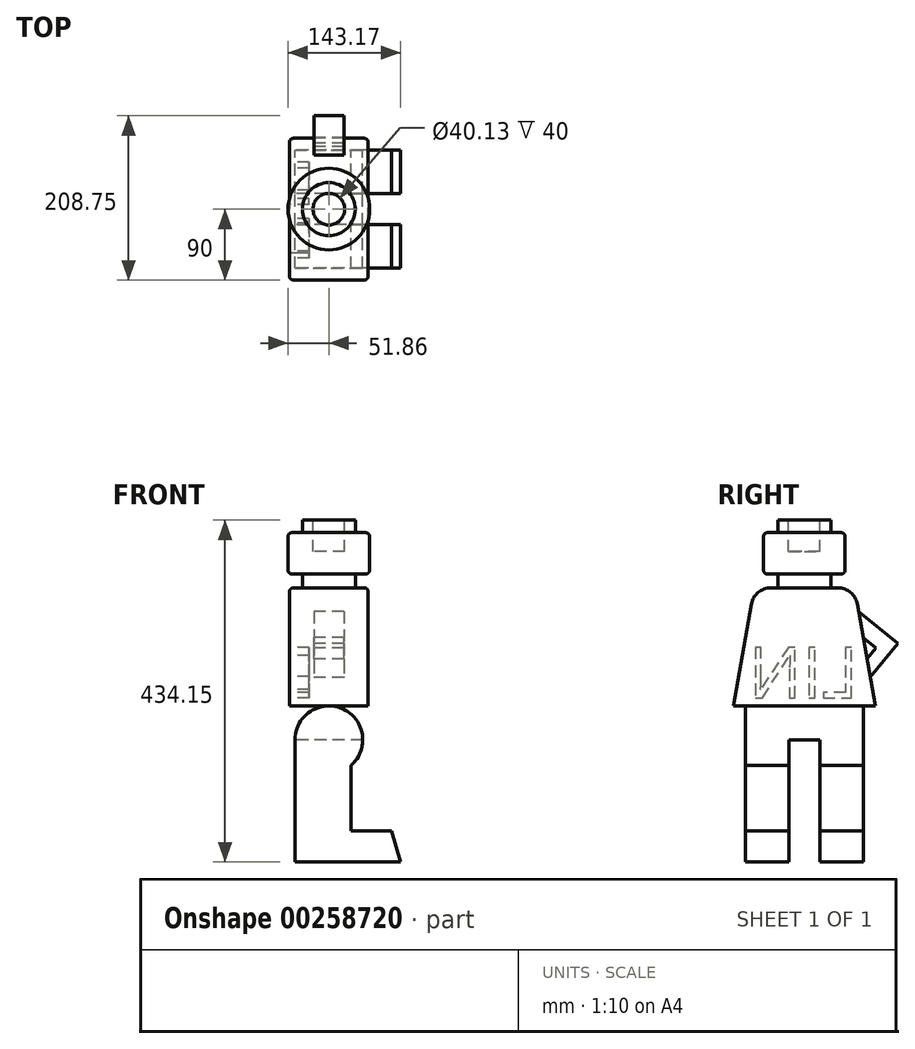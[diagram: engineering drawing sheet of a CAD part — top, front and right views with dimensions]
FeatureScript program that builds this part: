
annotation { "Feature Type Name" : "Feature", "Feature Type Description" : "" }
export const myFeature = defineFeature(function(context is Context, id is Id, definition is map)
    precondition{}
    {
        {
            var Q0;
            Q0=qCreatedBy(makeId("Front.planeOp"),FACE);
            var sketch = newSketch(context, id + "F0", { "sketchPlane" : qUnion([Q0])});
            skLineSegment(sketch, "E0", {"start": v(0, 41.34) * mm, "end": v(-33.6, 41.34) * mm});
            skLineSegment(sketch, "E1", {"start": v(-33.6, 41.34) * mm, "end": v(-33.6, 25.36) * mm});
            skLineSegment(sketch, "E2", {"start": v(-33.6, 25.36) * mm, "end": v(-51.86, 25.36) * mm});
            skLineSegment(sketch, "E3", {"start": v(-51.86, 25.36) * mm, "end": v(-51.86, -27.14) * mm});
            skLineSegment(sketch, "E4", {"start": v(-51.86, -27.14) * mm, "end": v(-33.6, -27.14) * mm});
            skLineSegment(sketch, "E5", {"start": v(-33.6, -27.14) * mm, "end": v(-33.6, -44.75) * mm});
            skLineSegment(sketch, "E6", {"start": v(-33.6, -44.75) * mm, "end": v(0, -44.75) * mm});
            skLineSegment(sketch, "E7", {"start": v(0, -44.75) * mm, "end": v(0, 41.34) * mm});
            skSolve(sketch);
        }
        {
            var Q0;
            Q0=makeQuery(id+"F0.imprint","IMPRINT",FACE,{"disambiguationData":[TD([[makeQuery(id+"F0.imprint","IMPRINT",EDGE,{"derivedFrom":sQuery(id+"F0.wireOp",EDGE,"E0")}),1.0]])]});
            var Q1;
            Q1=sQuery(id+"F0.wireOp",EDGE,"E7");
            revolve(context, id + "F1", {"entities" : qUnion([Q0]), "axis" : qUnion([Q1]), "revolveType" : RevolveType.FULL});
        }
        {
            var Q0;
            Q0=makeQuery(id+"F1.opRevolve","SWEPT_EDGE",EDGE,{"disambiguationData":[OSD([sQuery(id+"F0.wireOp",EDGE,"E2"),sQuery(id+"F0.wireOp",EDGE,"E3")])]});
            fillet(context, id + "F2", {"entities" : qUnion([Q0]), "radius" : 5 * mm, "tangentPropagation" : true, "allowEdgeOverflow" : false});
        }
        {
            var Q0;
            Q0=makeQuery(id+"F1.opRevolve","SWEPT_EDGE",EDGE,{"disambiguationData":[OSD([sQuery(id+"F0.wireOp",EDGE,"E3"),sQuery(id+"F0.wireOp",EDGE,"E4")])]});
            fillet(context, id + "F3", {"entities" : qUnion([Q0]), "radius" : 5 * mm, "tangentPropagation" : true, "allowEdgeOverflow" : false});
        }
        {
            var Q0;
            Q0=makeQuery(id+"F1.opRevolve","SWEPT_FACE",FACE,{"disambiguationData":[OSD([sQuery(id+"F0.wireOp",EDGE,"E0")])]});
            var sketch = newSketch(context, id + "F4", { "sketchPlane" : qUnion([Q0])});
            skCircle(sketch, "E8", {"center": v(0, 0) * mm, "radius": 20.06 * mm});
            skSolve(sketch);
        }
        {
            var Q0;
            Q0=makeQuery(id+"F4.imprint","IMPRINT",FACE,{"disambiguationData":[TD([[makeQuery(id+"F4.imprint","IMPRINT",EDGE,{"derivedFrom":sQuery(id+"F4.wireOp",EDGE,"E8")}),1.0]])]});
            extrude(context, id + "F5", {"entities" : qUnion([Q0]), "operationType" : NewBodyOperationType.REMOVE, "oppositeDirection" : true, "depth" : 40 * mm});
        }
        {
            var Q0;
            Q0=qCreatedBy(makeId("Right.planeOp"),FACE);
            var sketch = newSketch(context, id + "F6", { "sketchPlane" : qUnion([Q0])});
            skLineSegment(sketch, "E9.0", {"start": v(33.6, 41.34) * mm, "end": v(-33.6, 41.34) * mm});
            skLineSegment(sketch, "E10.0", {"start": v(33.6, -44.75) * mm, "end": v(-33.6, -44.75) * mm});
            skLineSegment(sketch, "E11", {"start": v(33.6, -44.75) * mm, "end": v(63.6, -44.75) * mm});
            skLineSegment(sketch, "E12", {"start": v(63.6, -44.75) * mm, "end": v(90, -194.47) * mm});
            skLineSegment(sketch, "E13", {"start": v(90, -194.47) * mm, "end": v(-90, -194.47) * mm});
            skLineSegment(sketch, "E14", {"start": v(-90, -194.47) * mm, "end": v(-63.6, -44.75) * mm});
            skLineSegment(sketch, "E15", {"start": v(-63.6, -44.75) * mm, "end": v(-33.6, -44.75) * mm});
            skSolve(sketch);
        }
        {
            var Q0;
            Q0=makeQuery(id+"F6.imprint","IMPRINT",FACE,{"disambiguationData":[TD([[makeQuery(id+"F6.imprint","IMPRINT",EDGE,{"derivedFrom":sQuery(id+"F6.wireOp",EDGE,"E10.0")}),1.0]])]});
            extrude(context, id + "F7", {"entities" : qUnion([Q0]), "endBound" : BoundingType.SYMMETRIC, "depth" : 100 * mm});
        }
        {
            var Q0;
            Q0=makeQuery(id+"F7.opExtrude","SWEPT_EDGE",EDGE,{"disambiguationData":[OSD([sQuery(id+"F6.wireOp",EDGE,"E14"),sQuery(id+"F6.wireOp",EDGE,"E15")])]});
            fillet(context, id + "F8", {"entities" : qUnion([Q0]), "radius" : 25 * mm, "tangentPropagation" : true, "allowEdgeOverflow" : false});
        }
        {
            var Q0;
            Q0=makeQuery(id+"F7.opExtrude","SWEPT_EDGE",EDGE,{"disambiguationData":[OSD([sQuery(id+"F6.wireOp",EDGE,"E11"),sQuery(id+"F6.wireOp",EDGE,"E12")])]});
            fillet(context, id + "F9", {"entities" : qUnion([Q0]), "radius" : 25 * mm, "tangentPropagation" : true, "allowEdgeOverflow" : false});
        }
        {
            var Q0;
            Q0=makeQuery(id+"F7.opExtrude","CAP_EDGE",EDGE,{"disambiguationData":[OSD([sQuery(id+"F6.wireOp",EDGE,"E10.0"),sQuery(id+"F6.wireOp",EDGE,"E11"),sQuery(id+"F6.wireOp",EDGE,"E15")])],"isStart":false});
            var Q1;
            Q1=makeQuery(id+"F7.opExtrude","CAP_EDGE",EDGE,{"disambiguationData":[OSD([sQuery(id+"F6.wireOp",EDGE,"E10.0"),sQuery(id+"F6.wireOp",EDGE,"E11"),sQuery(id+"F6.wireOp",EDGE,"E15")])],"isStart":true});
            fillet(context, id + "F10", {"entities" : qUnion([Q0, Q1]), "radius" : 5 * mm, "tangentPropagation" : true, "allowEdgeOverflow" : false});
        }
        {
            var Q0;
            Q0=makeQuery(id+"F7.opExtrude","CAP_FACE",FACE,{"disambiguationData":[OSD([sQuery(id+"F6.wireOp",EDGE,"E10.0"),sQuery(id+"F6.wireOp",EDGE,"E11"),sQuery(id+"F6.wireOp",EDGE,"E12"),sQuery(id+"F6.wireOp",EDGE,"E13"),sQuery(id+"F6.wireOp",EDGE,"E14"),sQuery(id+"F6.wireOp",EDGE,"E15")])],"isStart":true});
            var sketch = newSketch(context, id + "F11", { "sketchPlane" : qUnion([Q0])});
            skText(sketch, "E16", { "text": "LIN", "fontName": "OpenSans-Regular.ttf"});
            const initialGuessF11  = {"E16": [-0.06877, -0.18448, 1, 0, 0.06473]};
            skSetInitialGuess(sketch, initialGuessF11);
            skSolve(sketch);
        }
        {
            var Q0;
            Q0 = qSketchRegion(id + "F11", true);
            extrude(context, id + "F12", {"entities" : qUnion([Q0]), "operationType" : NewBodyOperationType.REMOVE, "oppositeDirection" : true, "depth" : 25 * mm});
        }
        {
            var Q0;
            Q0=qCreatedBy(makeId("Front.planeOp"),FACE);
            var sketch = newSketch(context, id + "F13", { "sketchPlane" : qUnion([Q0])});
            skPoint(sketch, "E17.0", {"position": v(0, -194.47) * mm});
            skArc(sketch, "E18", {"start": v(28.3, -270.17) * mm, "mid": v(17.8, -198.58) * mm, "end": v(-43.03, -237.75) * mm});
            skLineSegment(sketch, "E19", {"start": v(-43.03, -237.75) * mm, "end": v(-43.03, -392.8) * mm});
            skLineSegment(sketch, "E20", {"start": v(-43.03, -392.8) * mm, "end": v(91.3, -392.8) * mm});
            skLineSegment(sketch, "E21", {"start": v(91.3, -392.8) * mm, "end": v(79.54, -353.47) * mm});
            skLineSegment(sketch, "E22", {"start": v(79.54, -353.47) * mm, "end": v(28.3, -353.47) * mm});
            skLineSegment(sketch, "E23", {"start": v(28.3, -353.47) * mm, "end": v(28.3, -270.17) * mm});
            skSolve(sketch);
        }
        {
            var Q0;
            Q0=makeQuery(id+"F13.imprint","IMPRINT",FACE,{"disambiguationData":[TD([[makeQuery(id+"F13.imprint","IMPRINT",EDGE,{"derivedFrom":sQuery(id+"F13.wireOp",EDGE,"E18")}),1.0]])]});
            extrude(context, id + "F14", {"entities" : qUnion([Q0]), "endBound" : BoundingType.SYMMETRIC, "depth" : 150 * mm});
        }
        {
            var Q0;
            Q0=makeQuery(id+"F14.opExtrude","SWEPT_FACE",FACE,{"disambiguationData":[OSD([sQuery(id+"F13.wireOp",EDGE,"E19")])]});
            var sketch = newSketch(context, id + "F15", { "sketchPlane" : qUnion([Q0])});
            skLineSegment(sketch, "E24.bottom", {"start": v(-19.78, -191.01) * mm, "end": v(19.78, -191.01) * mm});
            skLineSegment(sketch, "E24.top", {"start": v(-19.78, -594.6) * mm, "end": v(19.78, -594.6) * mm});
            skLineSegment(sketch, "E24.left", {"start": v(-19.78, -191.01) * mm, "end": v(-19.78, -594.6) * mm});
            skLineSegment(sketch, "E24.right", {"start": v(19.78, -191.01) * mm, "end": v(19.78, -594.6) * mm});
            skPoint(sketch, "E24.middle", {"position": v(0, -392.8) * mm});
            skSolve(sketch);
        }
        {
            var Q0;
            {var subQ0=sQuery(id+"F15.wireOp",EDGE,"E24.left");var subQ1=sQuery(id+"F13.wireOp",EDGE,"E19");var subQ2=makeQuery(id+"F14.opExtrude","SWEPT_EDGE",EDGE,{"disambiguationData":[OSD([sQuery(id+"F13.wireOp",EDGE,"E18"),subQ1])]});var subQ3=makeQuery(id+"F15.imprint","INTERSECT",VERTEX,{"derivedFrom":[subQ2,subQ0]});Q0=makeQuery(id+"F15.imprint","IMPRINT",FACE,{"disambiguationData":[TD([[makeQuery(id+"F15.imprint","IMPRINT",EDGE,{"disambiguationData":[TD([[subQ3,-1.0]])],"derivedFrom":subQ0}),1.0]])]});}
            extrude(context, id + "F16", {"entities" : qUnion([Q0]), "operationType" : NewBodyOperationType.REMOVE, "oppositeDirection" : true, "depth" : 159 * mm});
        }
        {
            var Q0;
            Q0=qCreatedBy(makeId("Right.planeOp"),FACE);
            var sketch = newSketch(context, id + "F17", { "sketchPlane" : qUnion([Q0])});
            skLineSegment(sketch, "E25.0", {"start": v(67.24, -65.4) * mm, "end": v(90, -194.47) * mm});
            skArc(sketch, "E26.0", {"start": v(42.62, -44.75) * mm, "mid": v(58.7, -50.6) * mm, "end": v(67.24, -65.4) * mm});
            skLineSegment(sketch, "E27", {"start": v(68.88, -74.68) * mm, "end": v(118.75, -115.63) * mm});
            skLineSegment(sketch, "E28", {"start": v(118.75, -115.63) * mm, "end": v(83.64, -158.38) * mm});
            skLineSegment(sketch, "E29", {"start": v(83.64, -158.38) * mm, "end": v(79.52, -135.02) * mm});
            skLineSegment(sketch, "E30", {"start": v(79.52, -135.02) * mm, "end": v(91.09, -120.93) * mm});
            skLineSegment(sketch, "E31", {"start": v(91.09, -120.93) * mm, "end": v(74.65, -107.44) * mm});
            skSolve(sketch);
        }
        {
            var Q0;
            {var subQ0=sQuery(id+"F17.wireOp",EDGE,"E27");Q0=makeQuery(id+"F17.imprint","IMPRINT",FACE,{"disambiguationData":[TD([[makeQuery(id+"F17.imprint","IMPRINT",EDGE,{"derivedFrom":subQ0}),-1.0]])]});}
            extrude(context, id + "F18", {"entities" : qUnion([Q0]), "operationType" : NewBodyOperationType.ADD, "endBound" : BoundingType.SYMMETRIC, "depth" : 38 * mm});
        }
    });
